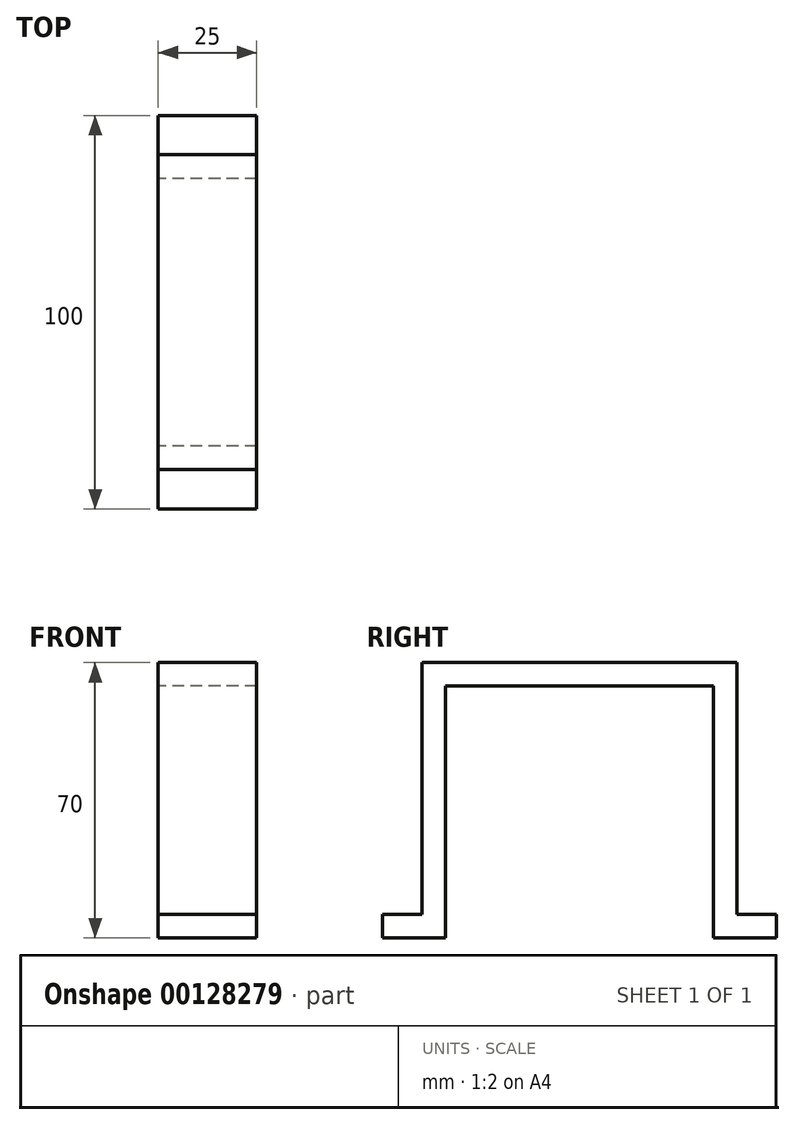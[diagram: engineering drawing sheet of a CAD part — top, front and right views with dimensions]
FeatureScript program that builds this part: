
annotation { "Feature Type Name" : "Feature", "Feature Type Description" : "" }
export const myFeature = defineFeature(function(context is Context, id is Id, definition is map)
    precondition{}
    {
        {
            var Q0;
            Q0=qCreatedBy(makeId("Right.planeOp"),FACE);
            var sketch = newSketch(context, id + "F0", { "sketchPlane" : qUnion([Q0])});
            skLineSegment(sketch, "E0", {"start": v(-50, 0) * mm, "end": v(-40, 0) * mm});
            skLineSegment(sketch, "E1", {"start": v(-40, 0) * mm, "end": v(-40, 64) * mm});
            skLineSegment(sketch, "E2", {"start": v(-40, 64) * mm, "end": v(40, 64) * mm});
            skLineSegment(sketch, "E3", {"start": v(40, 64) * mm, "end": v(40, 0) * mm});
            skLineSegment(sketch, "E4", {"start": v(40, 0) * mm, "end": v(50, 0) * mm});
            skLineSegment(sketch, "E5.0", {"start": v(-34, 58) * mm, "end": v(34, 58) * mm});
            skLineSegment(sketch, "E6.0", {"start": v(-34, -6) * mm, "end": v(-34, 58) * mm});
            skLineSegment(sketch, "E7.0", {"start": v(-50, -6) * mm, "end": v(-34, -6) * mm});
            skLineSegment(sketch, "E8.0", {"start": v(34, -6) * mm, "end": v(50, -6) * mm});
            skLineSegment(sketch, "E9.0", {"start": v(34, 58) * mm, "end": v(34, -6) * mm});
            skLineSegment(sketch, "E10", {"start": v(-50, -6) * mm, "end": v(-50, 0) * mm});
            skLineSegment(sketch, "E11", {"start": v(50, -6) * mm, "end": v(50, 0) * mm});
            skSolve(sketch);
        }
        {
            var Q0;
            Q0 = qSketchRegion(id + "F0", true);
            extrude(context, id + "F1", {"entities" : qUnion([Q0]), "depth" : 25 * mm});
        }
    });
